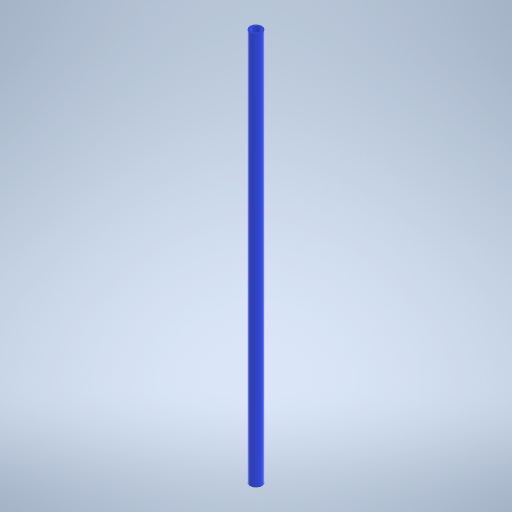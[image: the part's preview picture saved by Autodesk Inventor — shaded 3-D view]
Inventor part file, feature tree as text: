
AUTODESK INVENTOR PART (.ipt)
format: ipt  version: 2024.3 (Build 283343000, 343)  size: 236,032 bytes
history: native  units: mm
features: extrude x1, sketch x1
ambient origin geometry x8: Origin, YZ Plane, XZ Plane, XY Plane, X Axis, Y Axis, Z Axis, Center Point
bodies: Solid1 (feature_tree)
feature tree (2):
  extrude  "Extrusion1"  Depth=100.0mm
  sketch  "Sketch1"  dims[d0=3.0mm d1=2.0mm d2=100.0mm d3=0.0mm]
